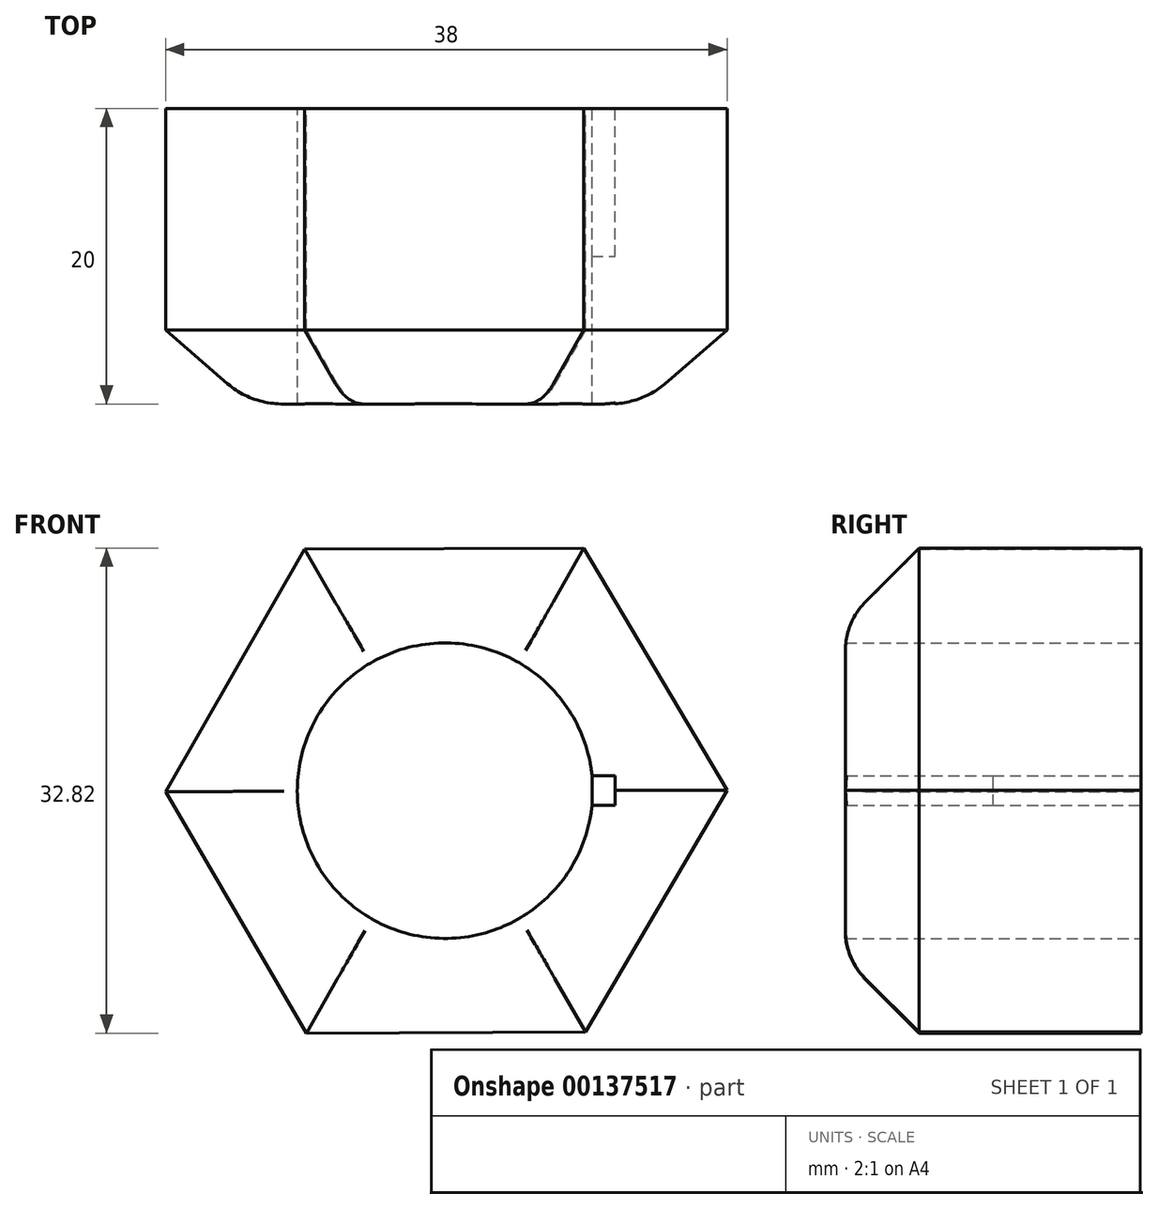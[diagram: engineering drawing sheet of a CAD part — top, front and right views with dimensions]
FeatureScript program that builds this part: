
annotation { "Feature Type Name" : "Feature", "Feature Type Description" : "" }
export const myFeature = defineFeature(function(context is Context, id is Id, definition is map)
    precondition{}
    {
        {
            var Q0;
            Q0=qCreatedBy(makeId("Front.planeOp"),FACE);
            var sketch = newSketch(context, id + "F0", { "sketchPlane" : qUnion([Q0])});
            skPoint(sketch, "E0.middle", {"position": v(0, 0) * mm});
            skArc(sketch, "E1", {"start": v(9.95, 1) * mm, "mid": v(-10, 0) * mm, "end": v(9.95, -1) * mm});
            skLineSegment(sketch, "E2.0", {"start": v(9.52, -16.34) * mm, "end": v(-9.4, -16.41) * mm});
            skLineSegment(sketch, "E2.1", {"start": v(-9.4, -16.41) * mm, "end": v(-18.9, -0.07) * mm});
            skLineSegment(sketch, "E2.2", {"start": v(-18.9, -0.07) * mm, "end": v(-9.52, 16.34) * mm});
            skLineSegment(sketch, "E2.3", {"start": v(-9.52, 16.34) * mm, "end": v(9.4, 16.41) * mm});
            skLineSegment(sketch, "E2.4", {"start": v(9.4, 16.41) * mm, "end": v(19.1, 0.03) * mm});
            skLineSegment(sketch, "E2.5", {"start": v(19.1, 0.03) * mm, "end": v(9.52, -16.34) * mm});
            skLineSegment(sketch, "E3.bottom", {"start": v(9.95, -1) * mm, "end": v(11.5, -1) * mm});
            skLineSegment(sketch, "E3.top", {"start": v(9.95, 1) * mm, "end": v(11.5, 1) * mm});
            skLineSegment(sketch, "E3.right", {"start": v(11.5, -1) * mm, "end": v(11.5, 1) * mm});
            skPoint(sketch, "E3.middle", {"position": v(10, 0) * mm});
            skPoint(sketch, "E4.orphan", {"position": v(8.5, 1) * mm});
            skPoint(sketch, "E5.orphan", {"position": v(8.5, -1) * mm});
            skLineSegment(sketch, "E6", {"start": v(9.95, 1) * mm, "end": v(9.95, -1) * mm});
            skSolve(sketch);
        }
        {
            var Q0;
            Q0 = qSketchRegion(id + "F0", true);
            extrude(context, id + "F1", {"entities" : qUnion([Q0]), "depth" : 20 * mm, "symmetric" : true});
        }
        {
            var Q0;
            Q0=makeQuery(id+"F1.opExtrude","CAP_EDGE",EDGE,{"disambiguationData":[OSD([sQuery(id+"F0.wireOp",EDGE,"E2.2")])],"isStart":false});
            var Q1;
            Q1=makeQuery(id+"F1.opExtrude","CAP_EDGE",EDGE,{"disambiguationData":[OSD([sQuery(id+"F0.wireOp",EDGE,"E2.1")])],"isStart":false});
            var Q2;
            Q2=makeQuery(id+"F1.opExtrude","CAP_EDGE",EDGE,{"disambiguationData":[OSD([sQuery(id+"F0.wireOp",EDGE,"E2.4")])],"isStart":false});
            var Q3;
            Q3=makeQuery(id+"F1.opExtrude","CAP_EDGE",EDGE,{"disambiguationData":[OSD([sQuery(id+"F0.wireOp",EDGE,"E2.0")])],"isStart":false});
            var Q4;
            Q4=makeQuery(id+"F1.opExtrude","CAP_EDGE",EDGE,{"disambiguationData":[OSD([sQuery(id+"F0.wireOp",EDGE,"E2.5")])],"isStart":false});
            var Q5;
            Q5=makeQuery(id+"F1.opExtrude","CAP_EDGE",EDGE,{"disambiguationData":[OSD([sQuery(id+"F0.wireOp",EDGE,"E2.3")])],"isStart":false});
            chamfer(context, id + "F2", {"entities" : qUnion([Q0, Q1, Q2, Q3, Q4, Q5]), "width" : 5 * mm, "tangentPropagation" : true});
        }
        {
            var Q0;
            {var subQ0=sQuery(id+"F0.wireOp",EDGE,"E2.2");Q0=makeQuery(id+"F2.opChamfer","BLEND_EDGE",EDGE,{"blendedFrom":[makeQuery(id+"F1.opExtrude","CAP_EDGE",EDGE,{"disambiguationData":[OSD([subQ0])],"isStart":false}),makeQuery(id+"F1.opExtrude","CAP_FACE",FACE,{"disambiguationData":[OSD([sQuery(id+"F0.wireOp",EDGE,"E1"),sQuery(id+"F0.wireOp",EDGE,"E2.0"),sQuery(id+"F0.wireOp",EDGE,"E2.1"),subQ0,sQuery(id+"F0.wireOp",EDGE,"E2.3"),sQuery(id+"F0.wireOp",EDGE,"E2.4"),sQuery(id+"F0.wireOp",EDGE,"E2.5")])],"isStart":false})],"blendedInto":[makeQuery(id+"F1.opExtrude","CAP_FACE",FACE,{"disambiguationData":[OSD([sQuery(id+"F0.wireOp",EDGE,"E1"),sQuery(id+"F0.wireOp",EDGE,"E2.0"),sQuery(id+"F0.wireOp",EDGE,"E2.1"),subQ0,sQuery(id+"F0.wireOp",EDGE,"E2.3"),sQuery(id+"F0.wireOp",EDGE,"E2.4"),sQuery(id+"F0.wireOp",EDGE,"E2.5")])],"isStart":false})]});}
            var Q1;
            {var subQ0=sQuery(id+"F0.wireOp",EDGE,"E2.1");Q1=makeQuery(id+"F2.opChamfer","BLEND_EDGE",EDGE,{"blendedFrom":[makeQuery(id+"F1.opExtrude","CAP_EDGE",EDGE,{"disambiguationData":[OSD([subQ0])],"isStart":false}),makeQuery(id+"F1.opExtrude","CAP_FACE",FACE,{"disambiguationData":[OSD([sQuery(id+"F0.wireOp",EDGE,"E1"),sQuery(id+"F0.wireOp",EDGE,"E2.0"),subQ0,sQuery(id+"F0.wireOp",EDGE,"E2.2"),sQuery(id+"F0.wireOp",EDGE,"E2.3"),sQuery(id+"F0.wireOp",EDGE,"E2.4"),sQuery(id+"F0.wireOp",EDGE,"E2.5")])],"isStart":false})],"blendedInto":[makeQuery(id+"F1.opExtrude","CAP_FACE",FACE,{"disambiguationData":[OSD([sQuery(id+"F0.wireOp",EDGE,"E1"),sQuery(id+"F0.wireOp",EDGE,"E2.0"),subQ0,sQuery(id+"F0.wireOp",EDGE,"E2.2"),sQuery(id+"F0.wireOp",EDGE,"E2.3"),sQuery(id+"F0.wireOp",EDGE,"E2.4"),sQuery(id+"F0.wireOp",EDGE,"E2.5")])],"isStart":false})]});}
            var Q2;
            {var subQ0=sQuery(id+"F0.wireOp",EDGE,"E2.3");Q2=makeQuery(id+"F2.opChamfer","BLEND_EDGE",EDGE,{"blendedFrom":[makeQuery(id+"F1.opExtrude","CAP_EDGE",EDGE,{"disambiguationData":[OSD([subQ0])],"isStart":false}),makeQuery(id+"F1.opExtrude","CAP_FACE",FACE,{"disambiguationData":[OSD([sQuery(id+"F0.wireOp",EDGE,"E1"),sQuery(id+"F0.wireOp",EDGE,"E2.0"),sQuery(id+"F0.wireOp",EDGE,"E2.1"),sQuery(id+"F0.wireOp",EDGE,"E2.2"),subQ0,sQuery(id+"F0.wireOp",EDGE,"E2.4"),sQuery(id+"F0.wireOp",EDGE,"E2.5")])],"isStart":false})],"blendedInto":[makeQuery(id+"F1.opExtrude","CAP_FACE",FACE,{"disambiguationData":[OSD([sQuery(id+"F0.wireOp",EDGE,"E1"),sQuery(id+"F0.wireOp",EDGE,"E2.0"),sQuery(id+"F0.wireOp",EDGE,"E2.1"),sQuery(id+"F0.wireOp",EDGE,"E2.2"),subQ0,sQuery(id+"F0.wireOp",EDGE,"E2.4"),sQuery(id+"F0.wireOp",EDGE,"E2.5")])],"isStart":false})]});}
            var Q3;
            {var subQ0=sQuery(id+"F0.wireOp",EDGE,"E2.4");Q3=makeQuery(id+"F2.opChamfer","BLEND_EDGE",EDGE,{"blendedFrom":[makeQuery(id+"F1.opExtrude","CAP_EDGE",EDGE,{"disambiguationData":[OSD([subQ0])],"isStart":false}),makeQuery(id+"F1.opExtrude","CAP_FACE",FACE,{"disambiguationData":[OSD([sQuery(id+"F0.wireOp",EDGE,"E1"),sQuery(id+"F0.wireOp",EDGE,"E2.0"),sQuery(id+"F0.wireOp",EDGE,"E2.1"),sQuery(id+"F0.wireOp",EDGE,"E2.2"),sQuery(id+"F0.wireOp",EDGE,"E2.3"),subQ0,sQuery(id+"F0.wireOp",EDGE,"E2.5")])],"isStart":false})],"blendedInto":[makeQuery(id+"F1.opExtrude","CAP_FACE",FACE,{"disambiguationData":[OSD([sQuery(id+"F0.wireOp",EDGE,"E1"),sQuery(id+"F0.wireOp",EDGE,"E2.0"),sQuery(id+"F0.wireOp",EDGE,"E2.1"),sQuery(id+"F0.wireOp",EDGE,"E2.2"),sQuery(id+"F0.wireOp",EDGE,"E2.3"),subQ0,sQuery(id+"F0.wireOp",EDGE,"E2.5")])],"isStart":false})]});}
            var Q4;
            {var subQ0=sQuery(id+"F0.wireOp",EDGE,"E2.5");Q4=makeQuery(id+"F2.opChamfer","BLEND_EDGE",EDGE,{"blendedFrom":[makeQuery(id+"F1.opExtrude","CAP_EDGE",EDGE,{"disambiguationData":[OSD([subQ0])],"isStart":false}),makeQuery(id+"F1.opExtrude","CAP_FACE",FACE,{"disambiguationData":[OSD([sQuery(id+"F0.wireOp",EDGE,"E1"),sQuery(id+"F0.wireOp",EDGE,"E2.0"),sQuery(id+"F0.wireOp",EDGE,"E2.1"),sQuery(id+"F0.wireOp",EDGE,"E2.2"),sQuery(id+"F0.wireOp",EDGE,"E2.3"),sQuery(id+"F0.wireOp",EDGE,"E2.4"),subQ0])],"isStart":false})],"blendedInto":[makeQuery(id+"F1.opExtrude","CAP_FACE",FACE,{"disambiguationData":[OSD([sQuery(id+"F0.wireOp",EDGE,"E1"),sQuery(id+"F0.wireOp",EDGE,"E2.0"),sQuery(id+"F0.wireOp",EDGE,"E2.1"),sQuery(id+"F0.wireOp",EDGE,"E2.2"),sQuery(id+"F0.wireOp",EDGE,"E2.3"),sQuery(id+"F0.wireOp",EDGE,"E2.4"),subQ0])],"isStart":false})]});}
            var Q5;
            {var subQ0=sQuery(id+"F0.wireOp",EDGE,"E2.0");Q5=makeQuery(id+"F2.opChamfer","BLEND_EDGE",EDGE,{"blendedFrom":[makeQuery(id+"F1.opExtrude","CAP_EDGE",EDGE,{"disambiguationData":[OSD([subQ0])],"isStart":false}),makeQuery(id+"F1.opExtrude","CAP_FACE",FACE,{"disambiguationData":[OSD([sQuery(id+"F0.wireOp",EDGE,"E1"),subQ0,sQuery(id+"F0.wireOp",EDGE,"E2.1"),sQuery(id+"F0.wireOp",EDGE,"E2.2"),sQuery(id+"F0.wireOp",EDGE,"E2.3"),sQuery(id+"F0.wireOp",EDGE,"E2.4"),sQuery(id+"F0.wireOp",EDGE,"E2.5")])],"isStart":false})],"blendedInto":[makeQuery(id+"F1.opExtrude","CAP_FACE",FACE,{"disambiguationData":[OSD([sQuery(id+"F0.wireOp",EDGE,"E1"),subQ0,sQuery(id+"F0.wireOp",EDGE,"E2.1"),sQuery(id+"F0.wireOp",EDGE,"E2.2"),sQuery(id+"F0.wireOp",EDGE,"E2.3"),sQuery(id+"F0.wireOp",EDGE,"E2.4"),sQuery(id+"F0.wireOp",EDGE,"E2.5")])],"isStart":false})]});}
            fillet(context, id + "F3", {"entities" : qUnion([Q0, Q1, Q2, Q3, Q4, Q5]), "radius" : 4.64 * mm, "tangentPropagation" : true, "allowEdgeOverflow" : false});
        }
        {
            var Q0;
            Q0=makeQuery(id+"F0.imprint","IMPRINT",FACE,{"disambiguationData":[TD([[makeQuery(id+"F0.imprint","IMPRINT",EDGE,{"derivedFrom":sQuery(id+"F0.wireOp",EDGE,"E3.bottom")}),1.0]])]});
            extrude(context, id + "F4", {"entities" : qUnion([Q0]), "operationType" : NewBodyOperationType.ADD, "depth" : 9.93 * mm});
        }
    });
